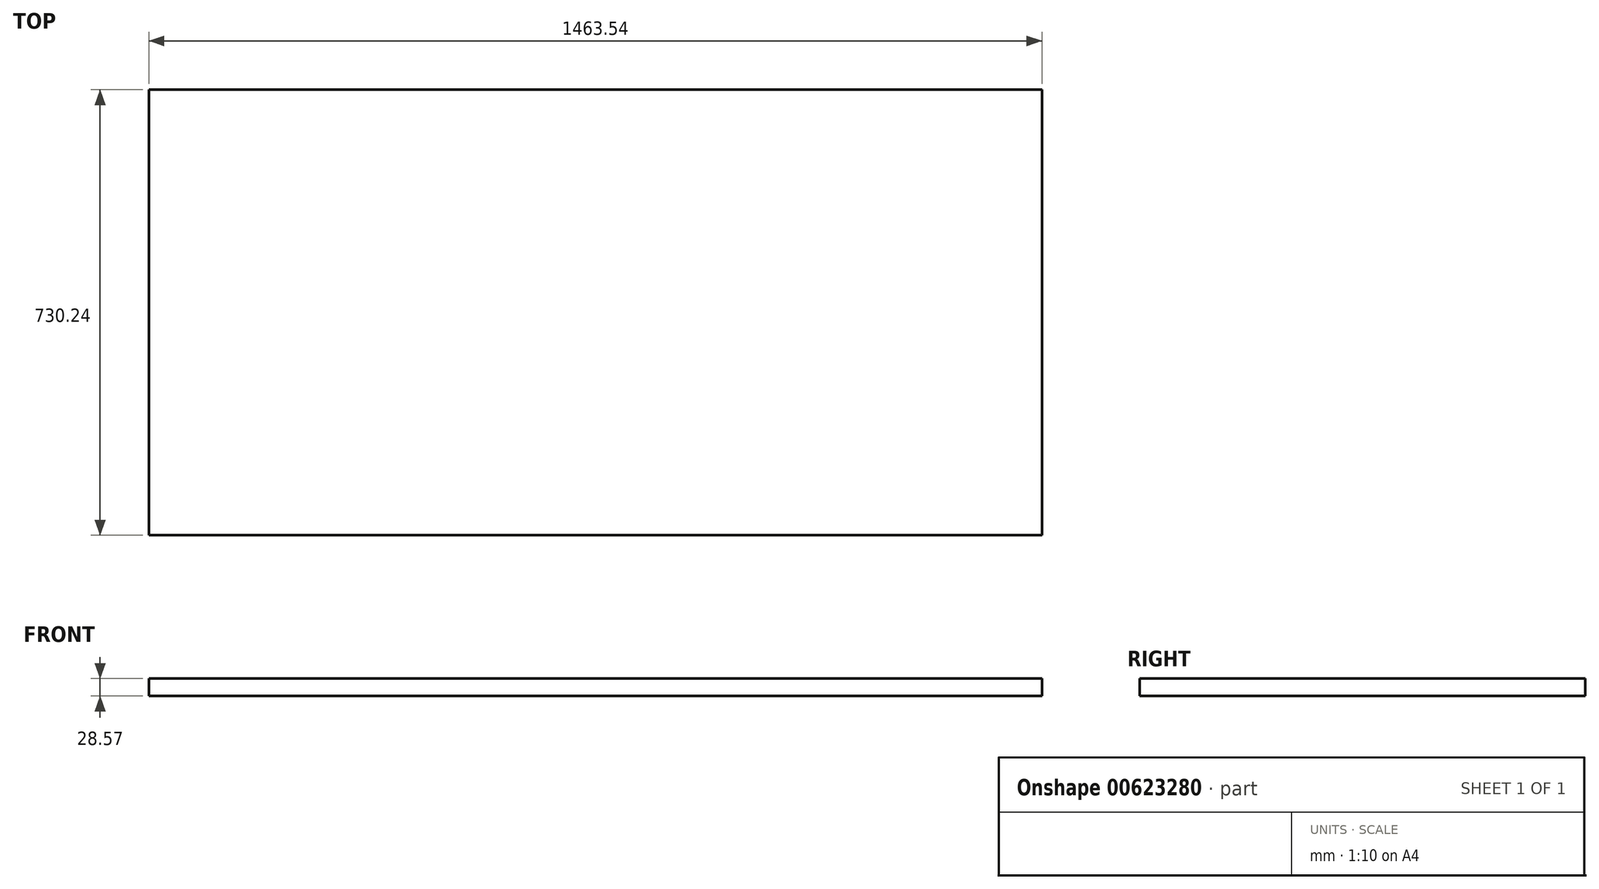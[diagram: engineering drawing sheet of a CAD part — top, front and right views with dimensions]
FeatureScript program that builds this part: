
annotation { "Feature Type Name" : "Feature", "Feature Type Description" : "" }
export const myFeature = defineFeature(function(context is Context, id is Id, definition is map)
    precondition{}
    {
        {
            var Q0;
            Q0=qCreatedBy(makeId("Top.planeOp"),FACE);
            var sketch = newSketch(context, id + "F0", { "sketchPlane" : qUnion([Q0])});
            skLineSegment(sketch, "E0.bottom", {"start": v(731.77, 365.12) * mm, "end": v(-731.77, 365.12) * mm});
            skLineSegment(sketch, "E0.top", {"start": v(731.77, -365.12) * mm, "end": v(-731.77, -365.13) * mm});
            skLineSegment(sketch, "E0.left", {"start": v(731.77, 365.13) * mm, "end": v(731.77, -365.13) * mm});
            skLineSegment(sketch, "E0.right", {"start": v(-731.77, 365.12) * mm, "end": v(-731.77, -365.13) * mm});
            skPoint(sketch, "E0.middle", {"position": v(0, 0) * mm});
            skSolve(sketch);
        }
        {
            var Q0;
            Q0=makeQuery(id+"F0.imprint","IMPRINT",FACE,{"disambiguationData":[TD([[makeQuery(id+"F0.imprint","IMPRINT",EDGE,{"derivedFrom":sQuery(id+"F0.wireOp",EDGE,"E0.bottom")}),1.0]])]});
            extrude(context, id + "F1", {"entities" : qUnion([Q0]), "depth" : 28.57 * mm, "offsetDistance" : 25.4 * mm});
        }
    });
